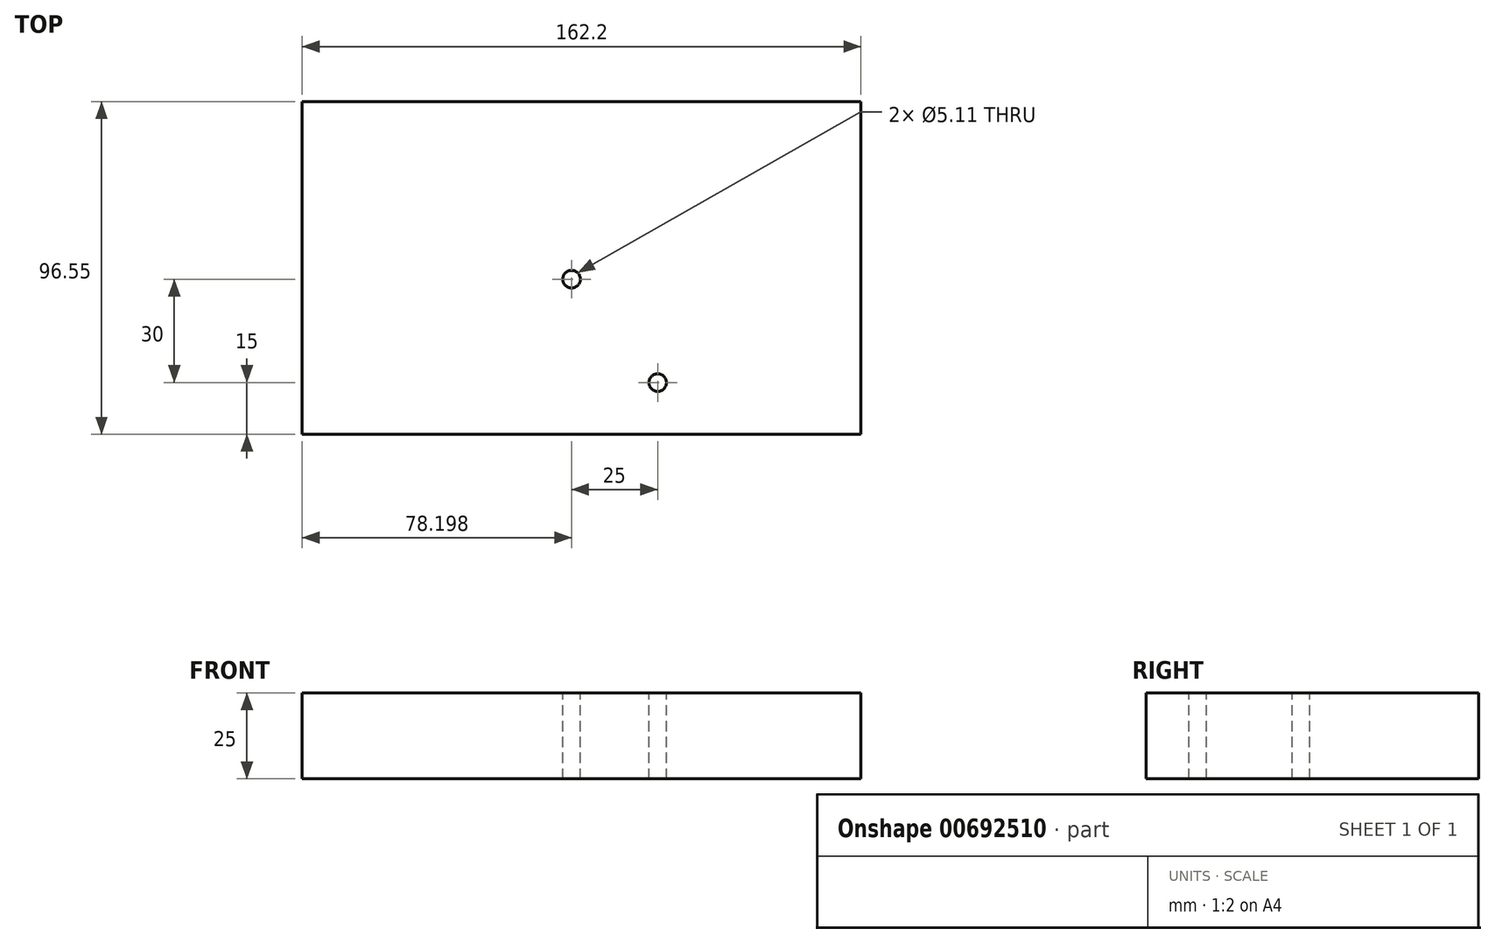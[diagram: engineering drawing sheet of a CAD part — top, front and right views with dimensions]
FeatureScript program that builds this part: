
annotation { "Feature Type Name" : "Feature", "Feature Type Description" : "" }
export const myFeature = defineFeature(function(context is Context, id is Id, definition is map)
    precondition{}
    {
        {
            var Q0;
            Q0=qCreatedBy(makeId("Top.planeOp"),FACE);
            var sketch = newSketch(context, id + "F0", { "sketchPlane" : qUnion([Q0])});
            skLineSegment(sketch, "E0.bottom", {"start": v(-33.53, 17.32) * mm, "end": v(128.67, 17.32) * mm});
            skLineSegment(sketch, "E0.top", {"start": v(-33.53, -79.23) * mm, "end": v(128.67, -79.23) * mm});
            skLineSegment(sketch, "E0.left", {"start": v(-33.53, 17.32) * mm, "end": v(-33.53, -79.23) * mm});
            skLineSegment(sketch, "E0.right", {"start": v(128.67, 17.32) * mm, "end": v(128.67, -79.23) * mm});
            skSolve(sketch);
        }
        {
            var Q0;
            Q0=makeQuery(id+"F0.imprint","IMPRINT",FACE,{"disambiguationData":[TD([[makeQuery(id+"F0.imprint","IMPRINT",EDGE,{"derivedFrom":sQuery(id+"F0.wireOp",EDGE,"E0.bottom")}),-1.0]])]});
            extrude(context, id + "F1", {"entities" : qUnion([Q0]), "depth" : 25 * mm, "offsetDistance" : 25 * mm});
        }
        {
            var Q0;
            Q0=makeQuery(id+"F1.opExtrude","CAP_FACE",FACE,{"disambiguationData":[OSD([sQuery(id+"F0.wireOp",EDGE,"E0.bottom"),sQuery(id+"F0.wireOp",EDGE,"E0.top"),sQuery(id+"F0.wireOp",EDGE,"E0.left"),sQuery(id+"F0.wireOp",EDGE,"E0.right")])],"isStart":false});
            var sketch = newSketch(context, id + "F2", { "sketchPlane" : qUnion([Q0])});
            skPoint(sketch, "E1", {"position": v(44.67, -34.23) * mm});
            skPoint(sketch, "E2", {"position": v(69.67, -64.23) * mm});
            skSolve(sketch);
        }
        {
            var Q0;
            Q0=sQuery(id+"F2.wireOp",VERTEX,"E1");
            var Q1;
            Q1=sQuery(id+"F2.wireOp",VERTEX,"E2");
            var Q2;
            Q2=makeQuery(id+"F1.opExtrude","SWEPT_BODY",BODY,{"disambiguationData":[OSD([sQuery(id+"F0.wireOp",EDGE,"E0.bottom"),sQuery(id+"F0.wireOp",EDGE,"E0.top"),sQuery(id+"F0.wireOp",EDGE,"E0.left"),sQuery(id+"F0.wireOp",EDGE,"E0.right")])]});
            hole(context, id + "F3", {"style" : HoleStyle.SIMPLE, "endStyle" : HoleEndStyle.THROUGH, "standardTappedOrClearance" : lookupTablePath({ "standard" : "ANSI", "engagement" : "75%", "pitch" : "20 tpi", "size" : "1/4", "type" : "Tapped" }), "standardBlindInLast" : lookupTablePath({ "standard" : "ANSI", "engagement" : "75%", "pitch" : "20 tpi", "size" : "1/4", "type" : "Tapped" }), "holeDiameter" : 5.1 * mm, "majorDiameter" : 6.35 * mm, "showTappedDepth" : true, "isTappedThrough" : true, "tappedDepth" : 12 * mm, "tapClearance" : 3, "locations" : qUnion([Q0, Q1]), "scope" : qUnion([Q2])});
        }
    });
